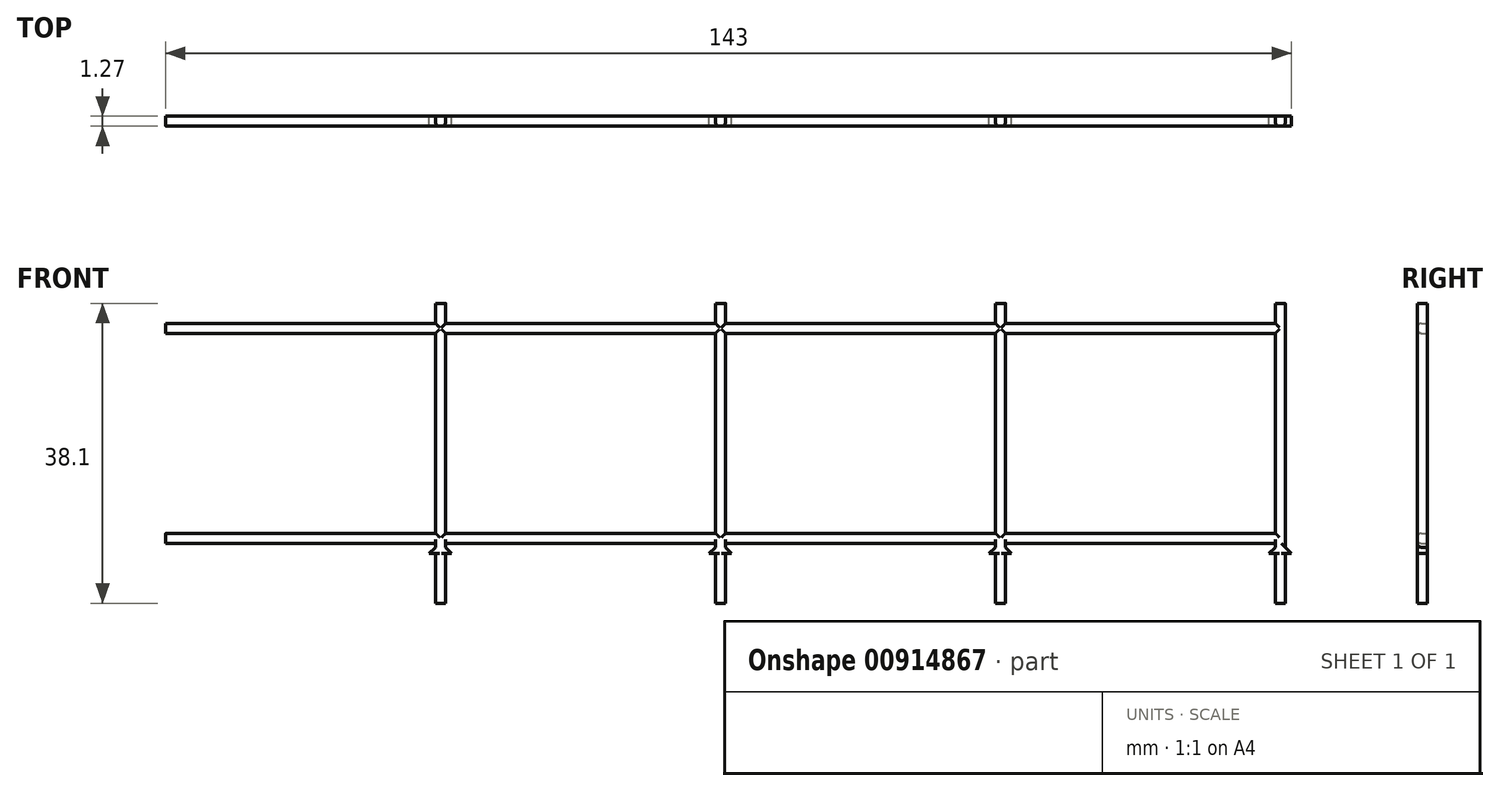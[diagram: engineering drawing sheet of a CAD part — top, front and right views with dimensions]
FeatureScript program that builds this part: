
annotation { "Feature Type Name" : "Feature", "Feature Type Description" : "" }
export const myFeature = defineFeature(function(context is Context, id is Id, definition is map)
    precondition{}
    {
        {
            var Q0;
            Q0=qCreatedBy(makeId("Front.planeOp"),FACE);
            var sketch = newSketch(context, id + "F0", { "sketchPlane" : qUnion([Q0])});
            skLineSegment(sketch, "E0", {"start": v(98.35, 38.1) * mm, "end": v(97.08, 38.1) * mm});
            skLineSegment(sketch, "E1", {"start": v(97.08, 38.1) * mm, "end": v(97.08, 35.56) * mm});
            skLineSegment(sketch, "E2", {"start": v(97.08, 35.56) * mm, "end": v(62.8, 35.56) * mm});
            skLineSegment(sketch, "E3", {"start": v(62.8, 34.3) * mm, "end": v(97.08, 34.3) * mm});
            skLineSegment(sketch, "E4", {"start": v(98.35, 0) * mm, "end": v(97.08, 0) * mm});
            skLineSegment(sketch, "E5", {"start": v(97.08, 7.62) * mm, "end": v(62.8, 7.62) * mm});
            skLineSegment(sketch, "E6", {"start": v(62.8, 8.9) * mm, "end": v(97.08, 8.9) * mm});
            skLineSegment(sketch, "E7", {"start": v(97.08, 8.9) * mm, "end": v(97.08, 34.3) * mm});
            skLineSegment(sketch, "E8", {"start": v(97.08, 0) * mm, "end": v(97.08, 6.35) * mm});
            skLineSegment(sketch, "E9", {"start": v(98.35, 0) * mm, "end": v(98.35, 6.35) * mm});
            skLineSegment(sketch, "E10", {"start": v(97.08, 6.35) * mm, "end": v(96.27, 6.35) * mm});
            skLineSegment(sketch, "E11", {"start": v(97.08, 7.62) * mm, "end": v(97.08, 7.12) * mm});
            skLineSegment(sketch, "E12", {"start": v(97.08, 7.12) * mm, "end": v(96.27, 6.35) * mm});
            skLineSegment(sketch, "E13", {"start": v(98.35, 6.35) * mm, "end": v(99.11, 6.35) * mm});
            skLineSegment(sketch, "E14", {"start": v(98.35, 38.1) * mm, "end": v(98.35, 7.12) * mm});
            skLineSegment(sketch, "E15", {"start": v(98.35, 7.12) * mm, "end": v(99.11, 6.35) * mm});
            skLineSegment(sketch, "E16.1.0.0", {"start": v(61.52, 0) * mm, "end": v(61.52, 6.35) * mm});
            skLineSegment(sketch, "E16.1.0.1", {"start": v(62.8, 38.1) * mm, "end": v(62.8, 7.12) * mm});
            skLineSegment(sketch, "E16.1.0.2", {"start": v(61.52, 8.9) * mm, "end": v(61.52, 34.3) * mm});
            skLineSegment(sketch, "E16.1.0.3", {"start": v(27.23, 34.3) * mm, "end": v(61.52, 34.3) * mm});
            skLineSegment(sketch, "E16.1.0.4", {"start": v(61.52, 7.62) * mm, "end": v(27.23, 7.62) * mm});
            skLineSegment(sketch, "E16.1.0.5", {"start": v(61.52, 38.1) * mm, "end": v(61.52, 35.56) * mm});
            skLineSegment(sketch, "E16.1.0.6", {"start": v(62.8, 0) * mm, "end": v(62.8, 6.35) * mm});
            skLineSegment(sketch, "E16.1.0.7", {"start": v(27.23, 8.9) * mm, "end": v(61.52, 8.9) * mm});
            skLineSegment(sketch, "E16.1.0.8", {"start": v(61.52, 35.56) * mm, "end": v(27.23, 35.56) * mm});
            skLineSegment(sketch, "E16.1.0.9", {"start": v(62.8, 7.12) * mm, "end": v(63.55, 6.35) * mm});
            skLineSegment(sketch, "E16.1.0.10", {"start": v(61.52, 6.35) * mm, "end": v(60.7, 6.35) * mm});
            skLineSegment(sketch, "E16.1.0.11", {"start": v(62.8, 6.35) * mm, "end": v(63.55, 6.35) * mm});
            skLineSegment(sketch, "E16.1.0.12", {"start": v(61.52, 7.12) * mm, "end": v(60.7, 6.35) * mm});
            skLineSegment(sketch, "E16.1.0.13", {"start": v(61.52, 7.62) * mm, "end": v(61.52, 7.12) * mm});
            skLineSegment(sketch, "E16.1.0.14", {"start": v(62.8, 38.1) * mm, "end": v(61.52, 38.1) * mm});
            skLineSegment(sketch, "E16.1.0.15", {"start": v(62.8, 0) * mm, "end": v(61.52, 0) * mm});
            skLineSegment(sketch, "E16.2.0.0", {"start": v(25.96, 0) * mm, "end": v(25.96, 6.35) * mm});
            skLineSegment(sketch, "E16.2.0.1", {"start": v(27.23, 38.1) * mm, "end": v(27.23, 7.12) * mm});
            skLineSegment(sketch, "E16.2.0.2", {"start": v(25.96, 8.9) * mm, "end": v(25.96, 34.3) * mm});
            skLineSegment(sketch, "E16.2.0.3", {"start": v(-8.33, 34.3) * mm, "end": v(25.96, 34.3) * mm});
            skLineSegment(sketch, "E16.2.0.4", {"start": v(25.96, 7.62) * mm, "end": v(-8.33, 7.62) * mm});
            skLineSegment(sketch, "E16.2.0.5", {"start": v(25.96, 38.1) * mm, "end": v(25.96, 35.56) * mm});
            skLineSegment(sketch, "E16.2.0.6", {"start": v(27.23, 0) * mm, "end": v(27.23, 6.35) * mm});
            skLineSegment(sketch, "E16.2.0.7", {"start": v(-8.33, 8.9) * mm, "end": v(25.96, 8.9) * mm});
            skLineSegment(sketch, "E16.2.0.8", {"start": v(25.96, 35.56) * mm, "end": v(-8.33, 35.56) * mm});
            skLineSegment(sketch, "E16.2.0.9", {"start": v(27.23, 7.12) * mm, "end": v(28, 6.35) * mm});
            skLineSegment(sketch, "E16.2.0.10", {"start": v(25.96, 6.35) * mm, "end": v(25.15, 6.35) * mm});
            skLineSegment(sketch, "E16.2.0.11", {"start": v(27.23, 6.35) * mm, "end": v(28, 6.35) * mm});
            skLineSegment(sketch, "E16.2.0.12", {"start": v(25.96, 7.12) * mm, "end": v(25.15, 6.35) * mm});
            skLineSegment(sketch, "E16.2.0.13", {"start": v(25.96, 7.62) * mm, "end": v(25.96, 7.12) * mm});
            skLineSegment(sketch, "E16.2.0.14", {"start": v(27.23, 38.1) * mm, "end": v(25.96, 38.1) * mm});
            skLineSegment(sketch, "E16.2.0.15", {"start": v(27.23, 0) * mm, "end": v(25.96, 0) * mm});
            skLineSegment(sketch, "E16.3.0.0", {"start": v(-9.6, 0) * mm, "end": v(-9.6, 6.35) * mm});
            skLineSegment(sketch, "E16.3.0.1", {"start": v(-8.33, 38.1) * mm, "end": v(-8.33, 7.12) * mm});
            skLineSegment(sketch, "E16.3.0.2", {"start": v(-9.6, 8.9) * mm, "end": v(-9.6, 34.3) * mm});
            skLineSegment(sketch, "E16.3.0.3", {"start": v(-43.89, 34.3) * mm, "end": v(-9.6, 34.3) * mm});
            skLineSegment(sketch, "E16.3.0.4", {"start": v(-9.6, 7.62) * mm, "end": v(-43.89, 7.62) * mm});
            skLineSegment(sketch, "E16.3.0.5", {"start": v(-9.6, 38.1) * mm, "end": v(-9.6, 35.56) * mm});
            skLineSegment(sketch, "E16.3.0.6", {"start": v(-8.33, 0) * mm, "end": v(-8.33, 6.35) * mm});
            skLineSegment(sketch, "E16.3.0.7", {"start": v(-43.89, 8.9) * mm, "end": v(-9.6, 8.9) * mm});
            skLineSegment(sketch, "E16.3.0.8", {"start": v(-9.6, 35.56) * mm, "end": v(-43.89, 35.56) * mm});
            skLineSegment(sketch, "E16.3.0.9", {"start": v(-8.33, 7.12) * mm, "end": v(-7.57, 6.35) * mm});
            skLineSegment(sketch, "E16.3.0.10", {"start": v(-9.6, 6.35) * mm, "end": v(-10.41, 6.35) * mm});
            skLineSegment(sketch, "E16.3.0.11", {"start": v(-8.33, 6.35) * mm, "end": v(-7.57, 6.35) * mm});
            skLineSegment(sketch, "E16.3.0.12", {"start": v(-9.6, 7.12) * mm, "end": v(-10.41, 6.35) * mm});
            skLineSegment(sketch, "E16.3.0.13", {"start": v(-9.6, 7.62) * mm, "end": v(-9.6, 7.12) * mm});
            skLineSegment(sketch, "E16.3.0.14", {"start": v(-8.33, 38.1) * mm, "end": v(-9.6, 38.1) * mm});
            skLineSegment(sketch, "E16.3.0.15", {"start": v(-8.33, 0) * mm, "end": v(-9.6, 0) * mm});
            skLineSegment(sketch, "E16.direction1", {"start": v(62.8, 7.62) * mm, "end": v(27.23, 7.62) * mm, "construction": true});
            skLineSegment(sketch, "E17", {"start": v(-43.89, 8.9) * mm, "end": v(-43.89, 7.62) * mm});
            skLineSegment(sketch, "E18", {"start": v(-43.89, 35.56) * mm, "end": v(-43.89, 34.3) * mm});
            skSolve(sketch);
        }
        {
            var Q0;
            Q0=makeQuery(id+"F0.imprint","IMPRINT",FACE,{"disambiguationData":[TD([[makeQuery(id+"F0.imprint","IMPRINT",EDGE,{"derivedFrom":sQuery(id+"F0.wireOp",EDGE,"E16.3.0.0")}),-1.0]])]});
            var Q1;
            Q1=makeQuery(id+"F0.imprint","IMPRINT",FACE,{"disambiguationData":[TD([[makeQuery(id+"F0.imprint","IMPRINT",EDGE,{"derivedFrom":sQuery(id+"F0.wireOp",EDGE,"E16.2.0.0")}),-1.0]])]});
            var Q2;
            Q2=makeQuery(id+"F0.imprint","IMPRINT",FACE,{"disambiguationData":[TD([[makeQuery(id+"F0.imprint","IMPRINT",EDGE,{"derivedFrom":sQuery(id+"F0.wireOp",EDGE,"E16.1.0.0")}),-1.0]])]});
            var Q3;
            Q3=makeQuery(id+"F0.imprint","IMPRINT",FACE,{"disambiguationData":[TD([[makeQuery(id+"F0.imprint","IMPRINT",EDGE,{"derivedFrom":sQuery(id+"F0.wireOp",EDGE,"E0")}),1.0]])]});
            extrude(context, id + "F1", {"entities" : qUnion([Q0, Q1, Q2, Q3]), "depth" : 1.27 * mm, "offsetDistance" : 25.4 * mm});
        }
        {
            var Q0;
            Q0=makeQuery(id+"F1.opExtrude","CAP_EDGE",EDGE,{"disambiguationData":[OSD([sQuery(id+"F0.wireOp",EDGE,"E16.3.0.3")])],"isStart":false});
            var Q1;
            Q1=makeQuery(id+"F1.opExtrude","CAP_EDGE",EDGE,{"disambiguationData":[OSD([sQuery(id+"F0.wireOp",EDGE,"E16.3.0.8")])],"isStart":false});
            var Q2;
            Q2=makeQuery(id+"F1.opExtrude","CAP_EDGE",EDGE,{"disambiguationData":[OSD([sQuery(id+"F0.wireOp",EDGE,"E16.3.0.2")])],"isStart":false});
            var Q3;
            {var subQ0=sQuery(id+"F0.wireOp",EDGE,"E16.3.0.1");Q3=makeQuery(id+"F1.opExtrude","CAP_EDGE",EDGE,{"disambiguationData":[OSD([subQ0]),TDD([makeQuery(id+"F0.imprint","IMPRINT",EDGE,{"disambiguationData":[TD([[makeQuery(id+"F0.imprint","INTERSECT",VERTEX,{"derivedFrom":[sQuery(id+"F0.wireOp",EDGE,"E16.2.0.3"),subQ0]}),-1.0]])],"derivedFrom":subQ0})])],"isStart":false});}
            var Q4;
            Q4=makeQuery(id+"F1.opExtrude","CAP_EDGE",EDGE,{"disambiguationData":[OSD([sQuery(id+"F0.wireOp",EDGE,"E16.3.0.7")])],"isStart":false});
            var Q5;
            Q5=makeQuery(id+"F1.opExtrude","CAP_EDGE",EDGE,{"disambiguationData":[OSD([sQuery(id+"F0.wireOp",EDGE,"E16.3.0.4")])],"isStart":false});
            var Q6;
            Q6=makeQuery(id+"F1.opExtrude","CAP_EDGE",EDGE,{"disambiguationData":[OSD([sQuery(id+"F0.wireOp",EDGE,"E16.3.0.5")])],"isStart":false});
            var Q7;
            Q7=makeQuery(id+"F1.opExtrude","CAP_EDGE",EDGE,{"disambiguationData":[OSD([sQuery(id+"F0.wireOp",EDGE,"E16.2.0.5")])],"isStart":false});
            var Q8;
            Q8=makeQuery(id+"F1.opExtrude","CAP_EDGE",EDGE,{"disambiguationData":[OSD([sQuery(id+"F0.wireOp",EDGE,"E16.1.0.5")])],"isStart":false});
            var Q9;
            {var subQ0=sQuery(id+"F0.wireOp",EDGE,"E16.2.0.1");Q9=makeQuery(id+"F1.opExtrude","CAP_EDGE",EDGE,{"disambiguationData":[OSD([subQ0]),TDD([makeQuery(id+"F0.imprint","IMPRINT",EDGE,{"disambiguationData":[TD([[makeQuery(id+"F0.imprint","INTERSECT",VERTEX,{"derivedFrom":[sQuery(id+"F0.wireOp",EDGE,"E16.1.0.8"),subQ0]}),1.0]])],"derivedFrom":subQ0})])],"isStart":false});}
            var Q10;
            {var subQ0=sQuery(id+"F0.wireOp",EDGE,"E16.3.0.1");Q10=makeQuery(id+"F1.opExtrude","CAP_EDGE",EDGE,{"disambiguationData":[OSD([subQ0]),TDD([makeQuery(id+"F0.imprint","IMPRINT",EDGE,{"disambiguationData":[TD([[makeQuery(id+"F0.imprint","INTERSECT",VERTEX,{"derivedFrom":[sQuery(id+"F0.wireOp",EDGE,"E16.2.0.8"),subQ0]}),1.0]])],"derivedFrom":subQ0})])],"isStart":false});}
            var Q11;
            Q11=makeQuery(id+"F1.opExtrude","CAP_EDGE",EDGE,{"disambiguationData":[OSD([sQuery(id+"F0.wireOp",EDGE,"E16.2.0.8")])],"isStart":false});
            var Q12;
            Q12=makeQuery(id+"F1.opExtrude","CAP_EDGE",EDGE,{"disambiguationData":[OSD([sQuery(id+"F0.wireOp",EDGE,"E16.2.0.3")])],"isStart":false});
            var Q13;
            Q13=makeQuery(id+"F1.opExtrude","CAP_EDGE",EDGE,{"disambiguationData":[OSD([sQuery(id+"F0.wireOp",EDGE,"E16.2.0.7")])],"isStart":false});
            var Q14;
            Q14=makeQuery(id+"F1.opExtrude","CAP_EDGE",EDGE,{"disambiguationData":[OSD([sQuery(id+"F0.wireOp",EDGE,"E16.2.0.4")])],"isStart":false});
            var Q15;
            Q15=makeQuery(id+"F1.opExtrude","CAP_EDGE",EDGE,{"disambiguationData":[OSD([sQuery(id+"F0.wireOp",EDGE,"E16.3.0.6")])],"isStart":false});
            var Q16;
            Q16=makeQuery(id+"F1.opExtrude","CAP_EDGE",EDGE,{"disambiguationData":[OSD([sQuery(id+"F0.wireOp",EDGE,"E16.2.0.6")])],"isStart":false});
            var Q17;
            Q17=makeQuery(id+"F1.opExtrude","CAP_EDGE",EDGE,{"disambiguationData":[OSD([sQuery(id+"F0.wireOp",EDGE,"E16.1.0.6")])],"isStart":false});
            var Q18;
            Q18=makeQuery(id+"F1.opExtrude","CAP_EDGE",EDGE,{"disambiguationData":[OSD([sQuery(id+"F0.wireOp",EDGE,"E16.1.0.4")])],"isStart":false});
            var Q19;
            Q19=makeQuery(id+"F1.opExtrude","CAP_EDGE",EDGE,{"disambiguationData":[OSD([sQuery(id+"F0.wireOp",EDGE,"E16.1.0.7")])],"isStart":false});
            var Q20;
            Q20=makeQuery(id+"F1.opExtrude","CAP_EDGE",EDGE,{"disambiguationData":[OSD([sQuery(id+"F0.wireOp",EDGE,"E16.1.0.3")])],"isStart":false});
            var Q21;
            Q21=makeQuery(id+"F1.opExtrude","CAP_EDGE",EDGE,{"disambiguationData":[OSD([sQuery(id+"F0.wireOp",EDGE,"E16.1.0.8")])],"isStart":false});
            var Q22;
            {var subQ0=sQuery(id+"F0.wireOp",EDGE,"E16.1.0.1");Q22=makeQuery(id+"F1.opExtrude","CAP_EDGE",EDGE,{"disambiguationData":[OSD([subQ0]),TDD([makeQuery(id+"F0.imprint","IMPRINT",EDGE,{"disambiguationData":[TD([[makeQuery(id+"F0.imprint","INTERSECT",VERTEX,{"derivedFrom":[sQuery(id+"F0.wireOp",EDGE,"E2"),subQ0]}),1.0]])],"derivedFrom":subQ0})])],"isStart":false});}
            var Q23;
            Q23=makeQuery(id+"F1.opExtrude","CAP_EDGE",EDGE,{"disambiguationData":[OSD([sQuery(id+"F0.wireOp",EDGE,"E2")])],"isStart":false});
            var Q24;
            Q24=makeQuery(id+"F1.opExtrude","CAP_EDGE",EDGE,{"disambiguationData":[OSD([sQuery(id+"F0.wireOp",EDGE,"E3")])],"isStart":false});
            var Q25;
            {var subQ0=sQuery(id+"F0.wireOp",EDGE,"E16.1.0.1");Q25=makeQuery(id+"F1.opExtrude","CAP_EDGE",EDGE,{"disambiguationData":[OSD([subQ0]),TDD([makeQuery(id+"F0.imprint","IMPRINT",EDGE,{"disambiguationData":[TD([[makeQuery(id+"F0.imprint","INTERSECT",VERTEX,{"derivedFrom":[sQuery(id+"F0.wireOp",EDGE,"E3"),subQ0]}),-1.0]])],"derivedFrom":subQ0})])],"isStart":false});}
            var Q26;
            Q26=makeQuery(id+"F1.opExtrude","CAP_EDGE",EDGE,{"disambiguationData":[OSD([sQuery(id+"F0.wireOp",EDGE,"E16.1.0.2")])],"isStart":false});
            var Q27;
            Q27=makeQuery(id+"F1.opExtrude","CAP_EDGE",EDGE,{"disambiguationData":[OSD([sQuery(id+"F0.wireOp",EDGE,"E6")])],"isStart":false});
            var Q28;
            Q28=makeQuery(id+"F1.opExtrude","CAP_EDGE",EDGE,{"disambiguationData":[OSD([sQuery(id+"F0.wireOp",EDGE,"E5")])],"isStart":false});
            var Q29;
            Q29=makeQuery(id+"F1.opExtrude","CAP_EDGE",EDGE,{"disambiguationData":[OSD([sQuery(id+"F0.wireOp",EDGE,"E16.1.0.0")])],"isStart":false});
            var Q30;
            Q30=makeQuery(id+"F1.opExtrude","CAP_EDGE",EDGE,{"disambiguationData":[OSD([sQuery(id+"F0.wireOp",EDGE,"E16.2.0.0")])],"isStart":false});
            var Q31;
            {var subQ0=sQuery(id+"F0.wireOp",EDGE,"E16.2.0.1");Q31=makeQuery(id+"F1.opExtrude","CAP_EDGE",EDGE,{"disambiguationData":[OSD([subQ0]),TDD([makeQuery(id+"F0.imprint","IMPRINT",EDGE,{"disambiguationData":[TD([[makeQuery(id+"F0.imprint","INTERSECT",VERTEX,{"derivedFrom":[sQuery(id+"F0.wireOp",EDGE,"E16.1.0.3"),subQ0]}),-1.0]])],"derivedFrom":subQ0})])],"isStart":false});}
            var Q32;
            Q32=makeQuery(id+"F1.opExtrude","CAP_EDGE",EDGE,{"disambiguationData":[OSD([sQuery(id+"F0.wireOp",EDGE,"E16.2.0.2")])],"isStart":false});
            var Q33;
            Q33=makeQuery(id+"F1.opExtrude","CAP_EDGE",EDGE,{"disambiguationData":[OSD([sQuery(id+"F0.wireOp",EDGE,"E16.3.0.0")])],"isStart":false});
            var Q34;
            Q34=makeQuery(id+"F1.opExtrude","CAP_EDGE",EDGE,{"disambiguationData":[OSD([sQuery(id+"F0.wireOp",EDGE,"E1")])],"isStart":false});
            var Q35;
            Q35=makeQuery(id+"F1.opExtrude","CAP_EDGE",EDGE,{"disambiguationData":[OSD([sQuery(id+"F0.wireOp",EDGE,"E7")])],"isStart":false});
            var Q36;
            Q36=makeQuery(id+"F1.opExtrude","CAP_EDGE",EDGE,{"disambiguationData":[OSD([sQuery(id+"F0.wireOp",EDGE,"E9")])],"isStart":false});
            var Q37;
            Q37=makeQuery(id+"F1.opExtrude","CAP_EDGE",EDGE,{"disambiguationData":[OSD([sQuery(id+"F0.wireOp",EDGE,"E14")])],"isStart":false});
            var Q38;
            Q38=makeQuery(id+"F1.opExtrude","CAP_EDGE",EDGE,{"disambiguationData":[OSD([sQuery(id+"F0.wireOp",EDGE,"E8")])],"isStart":false});
            fillet(context, id + "F2", {"entities" : qUnion([Q0, Q1, Q2, Q3, Q4, Q5, Q6, Q7, Q8, Q9, Q10, Q11, Q12, Q13, Q14, Q15, Q16, Q17, Q18, Q19, Q20, Q21, Q22, Q23, Q24, Q25, Q26, Q27, Q28, Q29, Q30, Q31, Q32, Q33, Q34, Q35, Q36, Q37, Q38]), "radius" : 0.5 * mm, "tangentPropagation" : true, "allowEdgeOverflow" : false});
        }
    });
